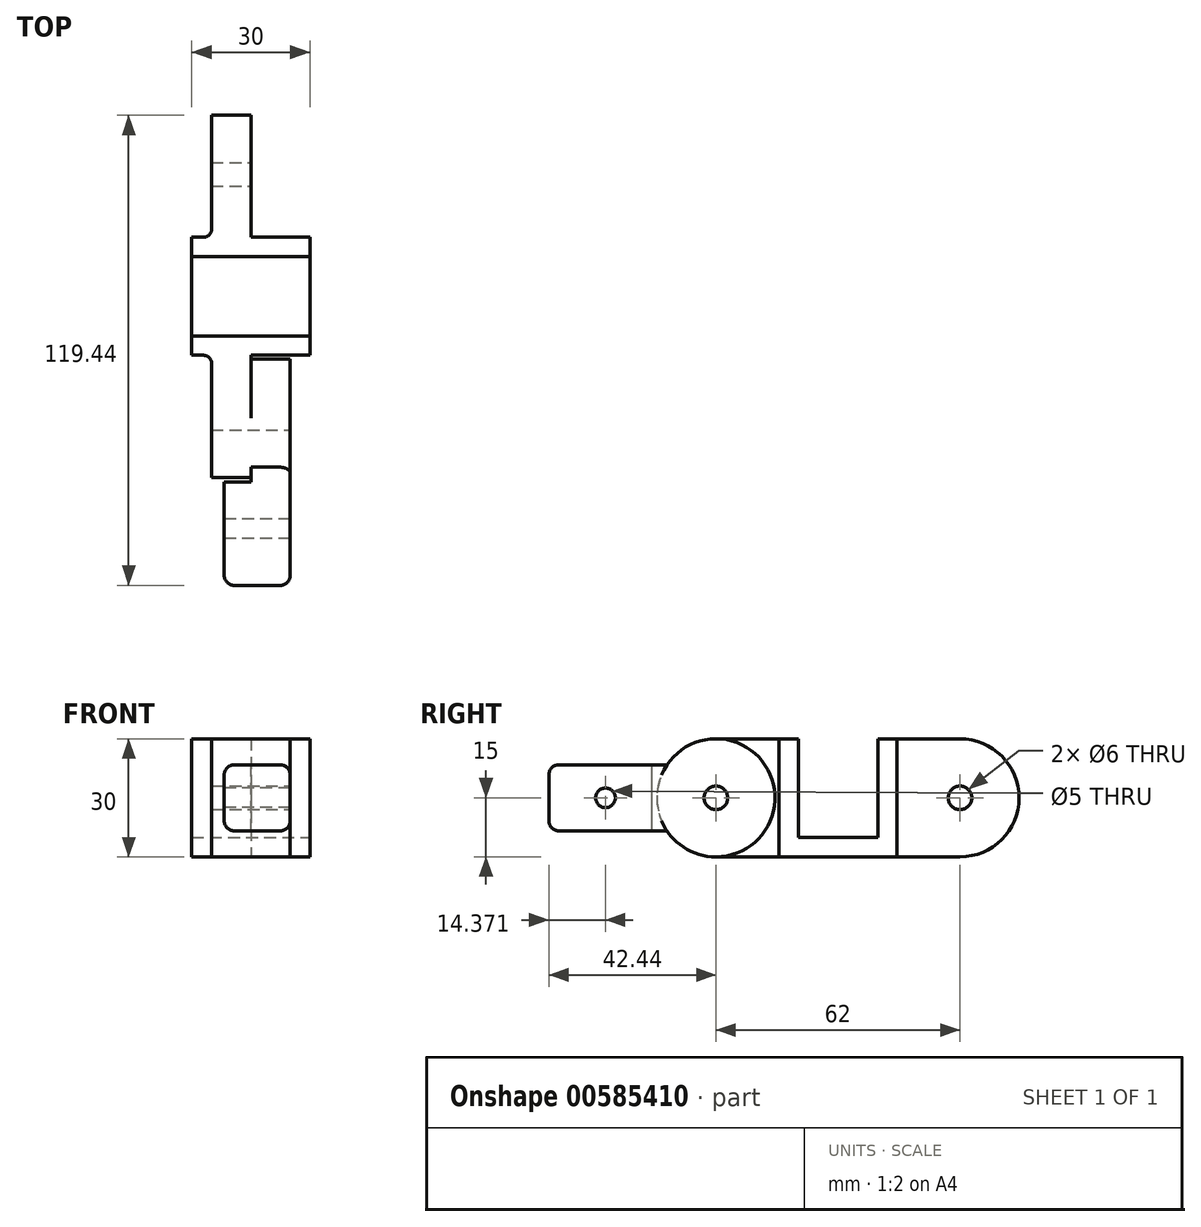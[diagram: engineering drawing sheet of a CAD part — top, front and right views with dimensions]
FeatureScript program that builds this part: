
annotation { "Feature Type Name" : "Feature", "Feature Type Description" : "" }
export const myFeature = defineFeature(function(context is Context, id is Id, definition is map)
    precondition{}
    {
        {
            assignVariable(context, id + "F0", {"name" : "Innen", "anyValue" : 16.75});
        }
        {
            var Q0;
            Q0=qCreatedBy(makeId("Top.planeOp"),FACE);
            var sketch = newSketch(context, id + "F1", { "sketchPlane" : qUnion([Q0])});
            skLineSegment(sketch, "E0.bottom", {"start": v(0, 0) * mm, "end": v(30, 0) * mm});
            skLineSegment(sketch, "E0.top", {"start": v(0, 30) * mm, "end": v(30, 30) * mm});
            skLineSegment(sketch, "E0.left", {"start": v(0, 0) * mm, "end": v(0, 30) * mm});
            skLineSegment(sketch, "E0.right", {"start": v(30, 0) * mm, "end": v(30, 30) * mm});
            skSolve(sketch);
        }
        {
            var Q0;
            Q0=makeQuery(id+"F1.imprint","IMPRINT",FACE,{"disambiguationData":[TD([[makeQuery(id+"F1.imprint","IMPRINT",EDGE,{"derivedFrom":sQuery(id+"F1.wireOp",EDGE,"E0.bottom")}),1.0]])]});
            extrude(context, id + "F2", {"entities" : qUnion([Q0]), "depth" : 5 * mm, "offsetDistance" : 25 * mm});
        }
        {
            var Q0;
            Q0=makeQuery(id+"F2.opExtrude","CAP_FACE",FACE,{"disambiguationData":[OSD([sQuery(id+"F1.wireOp",EDGE,"E0.bottom"),sQuery(id+"F1.wireOp",EDGE,"E0.top"),sQuery(id+"F1.wireOp",EDGE,"E0.left"),sQuery(id+"F1.wireOp",EDGE,"E0.right")])],"isStart":false});
            var sketch = newSketch(context, id + "F3", { "sketchPlane" : qUnion([Q0])});
            skLineSegment(sketch, "E1.bottom", {"start": v(0, 30) * mm, "end": v(30, 30) * mm});
            skLineSegment(sketch, "E1.top", {"start": v(0, 25.1) * mm, "end": v(30, 25.1) * mm});
            skLineSegment(sketch, "E1.left", {"start": v(0, 30) * mm, "end": v(0, 25.1) * mm});
            skLineSegment(sketch, "E1.right", {"start": v(30, 30) * mm, "end": v(30, 25.1) * mm});
            skLineSegment(sketch, "E2", {"start": v(0, 15) * mm, "end": v(30, 15) * mm, "construction": true});
            skLineSegment(sketch, "E3.MirrorCS", {"start": v(0, 0) * mm, "end": v(30, 0) * mm});
            skLineSegment(sketch, "E4.MirrorCS", {"start": v(0, 4.9) * mm, "end": v(30, 4.9) * mm});
            skLineSegment(sketch, "E5.MirrorCS", {"start": v(0, 0) * mm, "end": v(0, 4.9) * mm});
            skLineSegment(sketch, "E6.MirrorCS", {"start": v(30, 0) * mm, "end": v(30, 4.9) * mm});
            skSolve(sketch);
        }
        {
            var Q0;
            Q0=makeQuery(id+"F3.imprint","IMPRINT",FACE,{"disambiguationData":[TD([[makeQuery(id+"F3.imprint","IMPRINT",EDGE,{"derivedFrom":sQuery(id+"F3.wireOp",EDGE,"E1.bottom")}),-1.0]])]});
            var Q1;
            Q1=makeQuery(id+"F3.imprint","IMPRINT",FACE,{"disambiguationData":[TD([[makeQuery(id+"F3.imprint","IMPRINT",EDGE,{"derivedFrom":sQuery(id+"F3.wireOp",EDGE,"E3.MirrorCS")}),1.0]])]});
            extrude(context, id + "F4", {"entities" : qUnion([Q0, Q1]), "operationType" : NewBodyOperationType.ADD, "depth" : 25 * mm, "offsetDistance" : 25 * mm});
        }
        {
            var Q0;
            Q0=makeQuery(id+"F4.boolean.opBoolean","MERGE",FACE,{"derivedFrom":[makeQuery(id+"F2.opExtrude","SWEPT_FACE",FACE,{"disambiguationData":[OSD([sQuery(id+"F1.wireOp",EDGE,"E0.bottom")])]}),makeQuery(id+"F4.opExtrude","SWEPT_FACE",FACE,{"disambiguationData":[OSD([sQuery(id+"F3.wireOp",EDGE,"E3.MirrorCS")])]})]});
            var sketch = newSketch(context, id + "F5", { "sketchPlane" : qUnion([Q0])});
            skLineSegment(sketch, "E7", {"start": v(15, 30) * mm, "end": v(15, 0) * mm, "construction": true});
            skSolve(sketch);
        }
        {
            var Q0;
            Q0=sQuery(id+"F5.wireOp",EDGE,"E7");
            cPlane(context, id + "F6", {"entities" : qUnion([Q0]), "cplaneType" : CPlaneType.LINE_ANGLE, "offset" : 25 * mm, "angle" : 0 * degree, "width" : 150 * mm, "height" : 150 * mm});
        }
        {
            var Q0;
            Q0=qCreatedBy(id+"F6.planeOp",FACE);
            var sketch = newSketch(context, id + "F7", { "sketchPlane" : qUnion([Q0])});
            skLineSegment(sketch, "E8", {"start": v(0, 30) * mm, "end": v(0, 0) * mm});
            skLineSegment(sketch, "E9", {"start": v(0, 30) * mm, "end": v(16, 30) * mm});
            skLineSegment(sketch, "E10", {"start": v(16, 30) * mm, "end": v(16, 0) * mm});
            skLineSegment(sketch, "E11", {"start": v(16, 0) * mm, "end": v(0, 0) * mm});
            skPoint(sketch, "E12", {"position": v(16, 15) * mm});
            skArc(sketch, "E13", {"start": v(16, 0) * mm, "mid": v(23.05, 1.76) * mm, "end": v(28.44, 6.63) * mm});
            skArc(sketch, "E14", {"start": v(16, 0) * mm, "mid": v(1, 15) * mm, "end": v(16, 30) * mm});
            skLineSegment(sketch, "E15.left", {"start": v(16, 7) * mm, "end": v(16, 23) * mm});
            skPoint(sketch, "E16", {"position": v(28.44, 6.63) * mm});
            skPoint(sketch, "E17", {"position": v(28.44, 23.38) * mm});
            skLineSegment(sketch, "E18", {"start": v(28.44, 6.63) * mm, "end": v(28.44, 23.38) * mm});
            skArc(sketch, "E19.trimOffspring", {"start": v(28.44, 23.38) * mm, "mid": v(23.05, 28.24) * mm, "end": v(16, 30) * mm});
            skCircle(sketch, "E20", {"center": v(16, 15) * mm, "radius": 15 * mm});
            skLineSegment(sketch, "E21", {"start": v(0, 0) * mm, "end": v(-30, 0) * mm, "construction": true});
            skLineSegment(sketch, "E22", {"start": v(-15, 0) * mm, "end": v(-15, 50.51) * mm, "construction": true});
            skLineSegment(sketch, "E23.MirrorCS", {"start": v(-30, 30) * mm, "end": v(-46, 30) * mm});
            skCircle(sketch, "E24.MirrorC", {"center": v(-46, 15) * mm, "radius": 15 * mm});
            skLineSegment(sketch, "E25.MirrorCS", {"start": v(-46, 0) * mm, "end": v(-30, 0) * mm});
            skLineSegment(sketch, "E26.MirrorCS", {"start": v(-46, 30) * mm, "end": v(-46, 0) * mm});
            skLineSegment(sketch, "E27.MirrorCS", {"start": v(-58.44, 6.63) * mm, "end": v(-58.44, 23.38) * mm});
            skLineSegment(sketch, "E28.MirrorCS", {"start": v(-30, 30) * mm, "end": v(-30, 0) * mm});
            skSolve(sketch);
        }
        {
            var Q0;
            Q0=makeQuery(id+"F7.imprint","IMPRINT",FACE,{"disambiguationData":[TD([[makeQuery(id+"F7.imprint","IMPRINT",EDGE,{"derivedFrom":sQuery(id+"F7.wireOp",EDGE,"E8")}),1.0]])]});
            var Q1;
            {var subQ0=sQuery(id+"F7.wireOp",EDGE,"E13");Q1=makeQuery(id+"F7.imprint","IMPRINT",FACE,{"disambiguationData":[TD([[makeQuery(id+"F7.imprint","IMPRINT",EDGE,{"derivedFrom":subQ0}),1.0]])]});}
            var Q2;
            Q2=makeQuery(id+"F7.imprint","IMPRINT",FACE,{"disambiguationData":[TD([[makeQuery(id+"F7.imprint","IMPRINT",EDGE,{"derivedFrom":sQuery(id+"F7.wireOp",EDGE,"E10")}),-1.0]])]});
            var Q3;
            {var subQ1=sQuery(id+"F7.wireOp",EDGE,"E15.left");Q3=makeQuery(id+"F7.imprint","IMPRINT",FACE,{"disambiguationData":[TD([[makeQuery(id+"F7.imprint","IMPRINT",EDGE,{"derivedFrom":subQ1}),-1.0]])]});}
            var Q4;
            {var subQ0=sQuery(id+"F7.wireOp",EDGE,"E18");Q4=makeQuery(id+"F7.imprint","IMPRINT",FACE,{"disambiguationData":[TD([[makeQuery(id+"F7.imprint","IMPRINT",EDGE,{"derivedFrom":subQ0}),-1.0]])]});}
            var Q5;
            {var subQ0=sQuery(id+"F7.wireOp",EDGE,"E26.MirrorCS");Q5=makeQuery(id+"F7.imprint","IMPRINT",FACE,{"disambiguationData":[TD([[makeQuery(id+"F7.imprint","IMPRINT",EDGE,{"derivedFrom":subQ0}),-1.0]])]});}
            var Q6;
            {var subQ0=sQuery(id+"F7.wireOp",EDGE,"E26.MirrorCS");Q6=makeQuery(id+"F7.imprint","IMPRINT",FACE,{"disambiguationData":[TD([[makeQuery(id+"F7.imprint","IMPRINT",EDGE,{"derivedFrom":subQ0}),1.0]])]});}
            var Q7;
            {var subQ0=sQuery(id+"F7.wireOp",EDGE,"E23.MirrorCS");Q7=makeQuery(id+"F7.imprint","IMPRINT",FACE,{"disambiguationData":[TD([[makeQuery(id+"F7.imprint","IMPRINT",EDGE,{"derivedFrom":subQ0}),1.0]])]});}
            var Q8;
            {var subQ0=sQuery(id+"F7.wireOp",EDGE,"E27.MirrorCS");Q8=makeQuery(id+"F7.imprint","IMPRINT",FACE,{"disambiguationData":[TD([[makeQuery(id+"F7.imprint","IMPRINT",EDGE,{"derivedFrom":subQ0}),1.0]])]});}
            extrude(context, id + "F8", {"entities" : qUnion([Q0, Q1, Q2, Q3, Q4, Q5, Q6, Q7, Q8]), "operationType" : NewBodyOperationType.ADD, "depth" : 10 * mm, "offsetDistance" : 25 * mm});
        }
        {
            var Q0;
            Q0=makeQuery(id+"F8.opExtrude","CAP_EDGE",EDGE,{"disambiguationData":[OSD([sQuery(id+"F7.wireOp",EDGE,"E8")])],"isStart":false});
            var Q1;
            Q1=makeQuery(id+"F8.opExtrude","CAP_EDGE",EDGE,{"disambiguationData":[OSD([sQuery(id+"F7.wireOp",EDGE,"E8")])],"isStart":true});
            var Q2;
            Q2=makeQuery(id+"F8.opExtrude","CAP_EDGE",EDGE,{"disambiguationData":[OSD([sQuery(id+"F7.wireOp",EDGE,"E28.MirrorCS")])],"isStart":false});
            var Q3;
            Q3=makeQuery(id+"F8.opExtrude","CAP_EDGE",EDGE,{"disambiguationData":[OSD([sQuery(id+"F7.wireOp",EDGE,"E28.MirrorCS")])],"isStart":true});
            fillet(context, id + "F9", {"entities" : qUnion([Q0, Q1, Q2, Q3]), "radius" : 2 * mm, "tangentPropagation" : true, "allowEdgeOverflow" : false});
        }
        {
            var Q0;
            Q0=makeQuery(id+"F7.imprint","IMPRINT",FACE,{"disambiguationData":[TD([[makeQuery(id+"F7.imprint","IMPRINT",EDGE,{"derivedFrom":sQuery(id+"F7.wireOp",EDGE,"E10")}),-1.0]])]});
            var Q1;
            Q1=makeQuery(id+"F7.imprint","IMPRINT",FACE,{"disambiguationData":[TD([[makeQuery(id+"F7.imprint","IMPRINT",EDGE,{"derivedFrom":sQuery(id+"F7.wireOp",EDGE,"E10")}),1.0]])]});
            extrude(context, id + "F10", {"entities" : qUnion([Q0, Q1]), "oppositeDirection" : true, "depth" : 10 * mm, "offsetDistance" : 25 * mm});
        }
        {
            var Q0;
            Q0=makeQuery(id+"F10.opExtrude","SWEPT_FACE",FACE,{"disambiguationData":[OSD([sQuery(id+"F7.wireOp",EDGE,"E18")])]});
            extrude(context, id + "F11", {"entities" : qUnion([Q0]), "operationType" : NewBodyOperationType.ADD, "depth" : 30 * mm, "offsetDistance" : 25 * mm});
        }
        {
            var Q0;
            {var subQ0=sQuery(id+"F7.wireOp",EDGE,"E18");Q0=makeQuery(id+"F11.boolean.opBoolean","MERGE",FACE,{"derivedFrom":[makeQuery(id+"F10.opExtrude","CAP_FACE",FACE,{"disambiguationData":[OSD([subQ0,sQuery(id+"F7.wireOp",EDGE,"E20")])],"isStart":true}),makeQuery(id+"F11.opExtrude","SWEPT_FACE",FACE,{"disambiguationData":[OSD([subQ0]),TDD([makeQuery(id+"F10.opExtrude","CAP_EDGE",EDGE,{"disambiguationData":[OSD([subQ0])],"isStart":true})])]})]});}
            var sketch = newSketch(context, id + "F12", { "sketchPlane" : qUnion([Q0])});
            skLineSegment(sketch, "E29.bottom", {"start": v(58.44, 6.62) * mm, "end": v(32.2, 6.62) * mm});
            skLineSegment(sketch, "E29.top", {"start": v(58.44, 23.38) * mm, "end": v(32.2, 23.38) * mm});
            skLineSegment(sketch, "E29.left", {"start": v(58.44, 6.62) * mm, "end": v(58.44, 23.38) * mm});
            skLineSegment(sketch, "E29.right", {"start": v(32.2, 6.62) * mm, "end": v(32.2, 23.38) * mm});
            skSolve(sketch);
        }
        {
            var Q0;
            Q0=makeQuery(id+"F12.imprint","IMPRINT",FACE,{"disambiguationData":[TD([[makeQuery(id+"F12.imprint","IMPRINT",EDGE,{"derivedFrom":sQuery(id+"F12.wireOp",EDGE,"E29.bottom")}),-1.0]])]});
            extrude(context, id + "F13", {"entities" : qUnion([Q0]), "operationType" : NewBodyOperationType.ADD, "depth" : (getVariable(context, 'Innen') - 10) * mm, "offsetDistance" : 25 * mm});
        }
        {
            var Q0;
            {var subQ0=sQuery(id+"F7.wireOp",EDGE,"E18");Q0=makeQuery(id+"F11.boolean.opBoolean","MERGE",FACE,{"derivedFrom":[makeQuery(id+"F10.opExtrude","CAP_FACE",FACE,{"disambiguationData":[OSD([subQ0,sQuery(id+"F7.wireOp",EDGE,"E20")])],"isStart":false}),makeQuery(id+"F11.opExtrude","SWEPT_FACE",FACE,{"disambiguationData":[OSD([subQ0]),TDD([makeQuery(id+"F10.opExtrude","CAP_EDGE",EDGE,{"disambiguationData":[OSD([subQ0])],"isStart":false})])]})]});}
            var sketch = newSketch(context, id + "F14", { "sketchPlane" : qUnion([Q0])});
            skPoint(sketch, "E30", {"position": v(-16, 15) * mm});
            skCircle(sketch, "E31", {"center": v(-16, 15) * mm, "radius": 3 * mm});
            skCircle(sketch, "E32", {"center": v(46, 15) * mm, "radius": 3 * mm});
            skSolve(sketch);
        }
        {
            var Q0;
            Q0=makeQuery(id+"F14.imprint","IMPRINT",FACE,{"disambiguationData":[TD([[makeQuery(id+"F14.imprint","IMPRINT",EDGE,{"derivedFrom":sQuery(id+"F14.wireOp",EDGE,"E31")}),1.0]])]});
            var Q1;
            Q1=makeQuery(id+"F14.imprint","IMPRINT",FACE,{"disambiguationData":[TD([[makeQuery(id+"F14.imprint","IMPRINT",EDGE,{"derivedFrom":sQuery(id+"F14.wireOp",EDGE,"E32")}),1.0]])]});
            extrude(context, id + "F15", {"entities" : qUnion([Q0, Q1]), "operationType" : NewBodyOperationType.REMOVE, "oppositeDirection" : true, "depth" : 25 * mm, "offsetDistance" : 25 * mm});
        }
        {
            var Q0;
            Q0=makeQuery(id+"F13.opExtrude","CAP_EDGE",EDGE,{"disambiguationData":[OSD([sQuery(id+"F12.wireOp",EDGE,"E29.top")])],"isStart":false});
            var Q1;
            Q1=makeQuery(id+"F13.opExtrude","CAP_EDGE",EDGE,{"disambiguationData":[OSD([sQuery(id+"F12.wireOp",EDGE,"E29.bottom")])],"isStart":false});
            var Q2;
            {var subQ0=sQuery(id+"F7.wireOp",EDGE,"E20");var subQ1=sQuery(id+"F7.wireOp",EDGE,"E18");Q2=makeQuery(id+"F11.opExtrude","SWEPT_EDGE",EDGE,{"disambiguationData":[OSD([subQ1,subQ0]),TDD([makeQuery(id+"F10.opExtrude","CAP_VERTEX",VERTEX,{"disambiguationData":[OSD([subQ1,subQ0]),TDD([makeQuery(id+"F7.imprint","INTERSECT",VERTEX,{"disambiguationData":[OD(1.0)],"derivedFrom":[subQ1,subQ0]})])],"isStart":false})])]});}
            var Q3;
            {var subQ0=sQuery(id+"F7.wireOp",EDGE,"E20");var subQ1=sQuery(id+"F7.wireOp",EDGE,"E18");Q3=makeQuery(id+"F11.opExtrude","SWEPT_EDGE",EDGE,{"disambiguationData":[OSD([subQ1,subQ0]),TDD([makeQuery(id+"F10.opExtrude","CAP_VERTEX",VERTEX,{"disambiguationData":[OSD([subQ1,subQ0]),TDD([makeQuery(id+"F7.imprint","INTERSECT",VERTEX,{"disambiguationData":[OD(0.0)],"derivedFrom":[subQ1,subQ0]})])],"isStart":false})])]});}
            var Q4;
            {var subQ0=sQuery(id+"F7.wireOp",EDGE,"E18");Q4=makeQuery(id+"F11.opExtrude","CAP_EDGE",EDGE,{"disambiguationData":[OSD([subQ0]),TDD([makeQuery(id+"F10.opExtrude","CAP_EDGE",EDGE,{"disambiguationData":[OSD([subQ0])],"isStart":false})])],"isStart":false});}
            var Q5;
            Q5=makeQuery(id+"F13.opExtrude","CAP_EDGE",EDGE,{"disambiguationData":[OSD([sQuery(id+"F12.wireOp",EDGE,"E29.left")])],"isStart":false});
            var Q6;
            {var subQ0=sQuery(id+"F7.wireOp",EDGE,"E20");var subQ1=sQuery(id+"F7.wireOp",EDGE,"E18");Q6=makeQuery(id+"F13.boolean.opBoolean","MERGE",EDGE,{"derivedFrom":[makeQuery(id+"F11.opExtrude","CAP_EDGE",EDGE,{"disambiguationData":[OSD([subQ1,subQ0]),TDD([makeQuery(id+"F10.opExtrude","SWEPT_EDGE",EDGE,{"disambiguationData":[OSD([subQ1,subQ0]),TDD([makeQuery(id+"F7.imprint","INTERSECT",VERTEX,{"disambiguationData":[OD(0.0)],"derivedFrom":[subQ1,subQ0]})])]})])],"isStart":false}),makeQuery(id+"F13.opExtrude","SWEPT_EDGE",EDGE,{"disambiguationData":[OSD([sQuery(id+"F12.wireOp",EDGE,"E29.bottom"),sQuery(id+"F12.wireOp",EDGE,"E29.left")])]})]});}
            var Q7;
            {var subQ0=sQuery(id+"F7.wireOp",EDGE,"E20");var subQ1=sQuery(id+"F7.wireOp",EDGE,"E18");Q7=makeQuery(id+"F13.boolean.opBoolean","MERGE",EDGE,{"derivedFrom":[makeQuery(id+"F11.opExtrude","CAP_EDGE",EDGE,{"disambiguationData":[OSD([subQ1,subQ0]),TDD([makeQuery(id+"F10.opExtrude","SWEPT_EDGE",EDGE,{"disambiguationData":[OSD([subQ1,subQ0]),TDD([makeQuery(id+"F7.imprint","INTERSECT",VERTEX,{"disambiguationData":[OD(1.0)],"derivedFrom":[subQ1,subQ0]})])]})])],"isStart":false}),makeQuery(id+"F13.opExtrude","SWEPT_EDGE",EDGE,{"disambiguationData":[OSD([sQuery(id+"F12.wireOp",EDGE,"E29.top"),sQuery(id+"F12.wireOp",EDGE,"E29.left")])]})]});}
            fillet(context, id + "F16", {"entities" : qUnion([Q0, Q1, Q2, Q3, Q4, Q5, Q6, Q7]), "radius" : 2.5 * mm, "tangentPropagation" : true, "allowEdgeOverflow" : false});
        }
        {
            var Q0;
            Q0=makeQuery(id+"F13.opExtrude","CAP_FACE",FACE,{"disambiguationData":[OSD([sQuery(id+"F12.wireOp",EDGE,"E29.bottom"),sQuery(id+"F12.wireOp",EDGE,"E29.top"),sQuery(id+"F12.wireOp",EDGE,"E29.left"),sQuery(id+"F12.wireOp",EDGE,"E29.right")])],"isStart":false});
            var sketch = newSketch(context, id + "F17", { "sketchPlane" : qUnion([Q0])});
            skLineSegment(sketch, "E33", {"start": v(32.2, 20.88) * mm, "end": v(55.94, 9.12) * mm, "construction": true});
            skLineSegment(sketch, "E34", {"start": v(55.94, 20.88) * mm, "end": v(32.2, 9.12) * mm, "construction": true});
            skCircle(sketch, "E35", {"center": v(44.07, 15) * mm, "radius": 2.5 * mm});
            skSolve(sketch);
        }
        {
            var Q0;
            Q0=makeQuery(id+"F17.imprint","IMPRINT",FACE,{"disambiguationData":[TD([[makeQuery(id+"F17.imprint","IMPRINT",EDGE,{"derivedFrom":sQuery(id+"F17.wireOp",EDGE,"E35")}),1.0]])]});
            extrude(context, id + "F18", {"entities" : qUnion([Q0]), "operationType" : NewBodyOperationType.REMOVE, "endBound" : BoundingType.UP_TO_NEXT, "oppositeDirection" : true, "depth" : 25 * mm, "offsetDistance" : 25 * mm});
        }
    });
